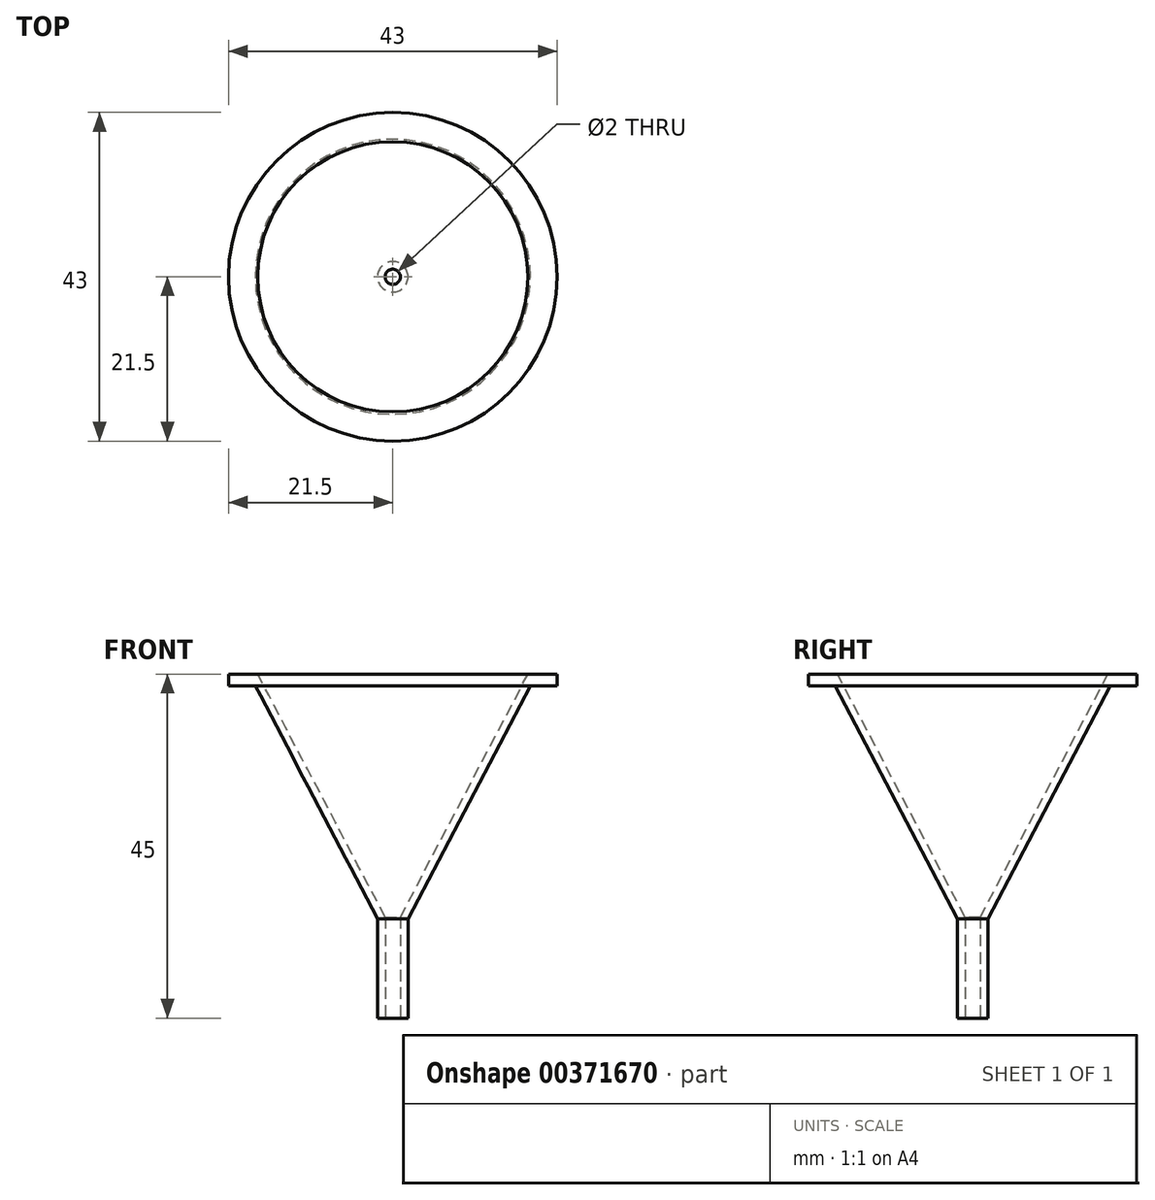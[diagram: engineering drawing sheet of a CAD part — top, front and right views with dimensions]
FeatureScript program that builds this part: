
annotation { "Feature Type Name" : "Feature", "Feature Type Description" : "" }
export const myFeature = defineFeature(function(context is Context, id is Id, definition is map)
    precondition{}
    {
        {
            var Q0;
            Q0=qCreatedBy(makeId("Front.planeOp"),FACE);
            var sketch = newSketch(context, id + "F0", { "sketchPlane" : qUnion([Q0])});
            skLineSegment(sketch, "E0", {"start": v(17.68, 45) * mm, "end": v(21.5, 45) * mm});
            skLineSegment(sketch, "E1", {"start": v(21.5, 45) * mm, "end": v(21.5, 43.5) * mm});
            skLineSegment(sketch, "E2", {"start": v(21.5, 43.5) * mm, "end": v(18, 43.5) * mm});
            skLineSegment(sketch, "E3", {"start": v(18, 43.5) * mm, "end": v(2, 13) * mm});
            skLineSegment(sketch, "E4", {"start": v(2, 13) * mm, "end": v(2, 0) * mm});
            skLineSegment(sketch, "E5", {"start": v(2, 0) * mm, "end": v(0, 0) * mm});
            skLineSegment(sketch, "E6", {"start": v(1, 0) * mm, "end": v(1, 13.21) * mm});
            skLineSegment(sketch, "E7", {"start": v(1, 13.21) * mm, "end": v(17.68, 45) * mm});
            skPoint(sketch, "E8.orphan", {"position": v(0, 45) * mm});
            skLineSegment(sketch, "E9", {"start": v(0, 0) * mm, "end": v(0, 45) * mm});
            skSolve(sketch);
        }
        {
            var Q0;
            Q0=makeQuery(id+"F0.imprint","IMPRINT",FACE,{"disambiguationData":[TD([[makeQuery(id+"F0.imprint","IMPRINT",EDGE,{"derivedFrom":sQuery(id+"F0.wireOp",EDGE,"E0")}),-1.0]])]});
            var Q1;
            Q1=sQuery(id+"F0.wireOp",EDGE,"E9");
            revolve(context, id + "F1", {"entities" : qUnion([Q0]), "axis" : qUnion([Q1]), "revolveType" : RevolveType.FULL});
        }
    });
